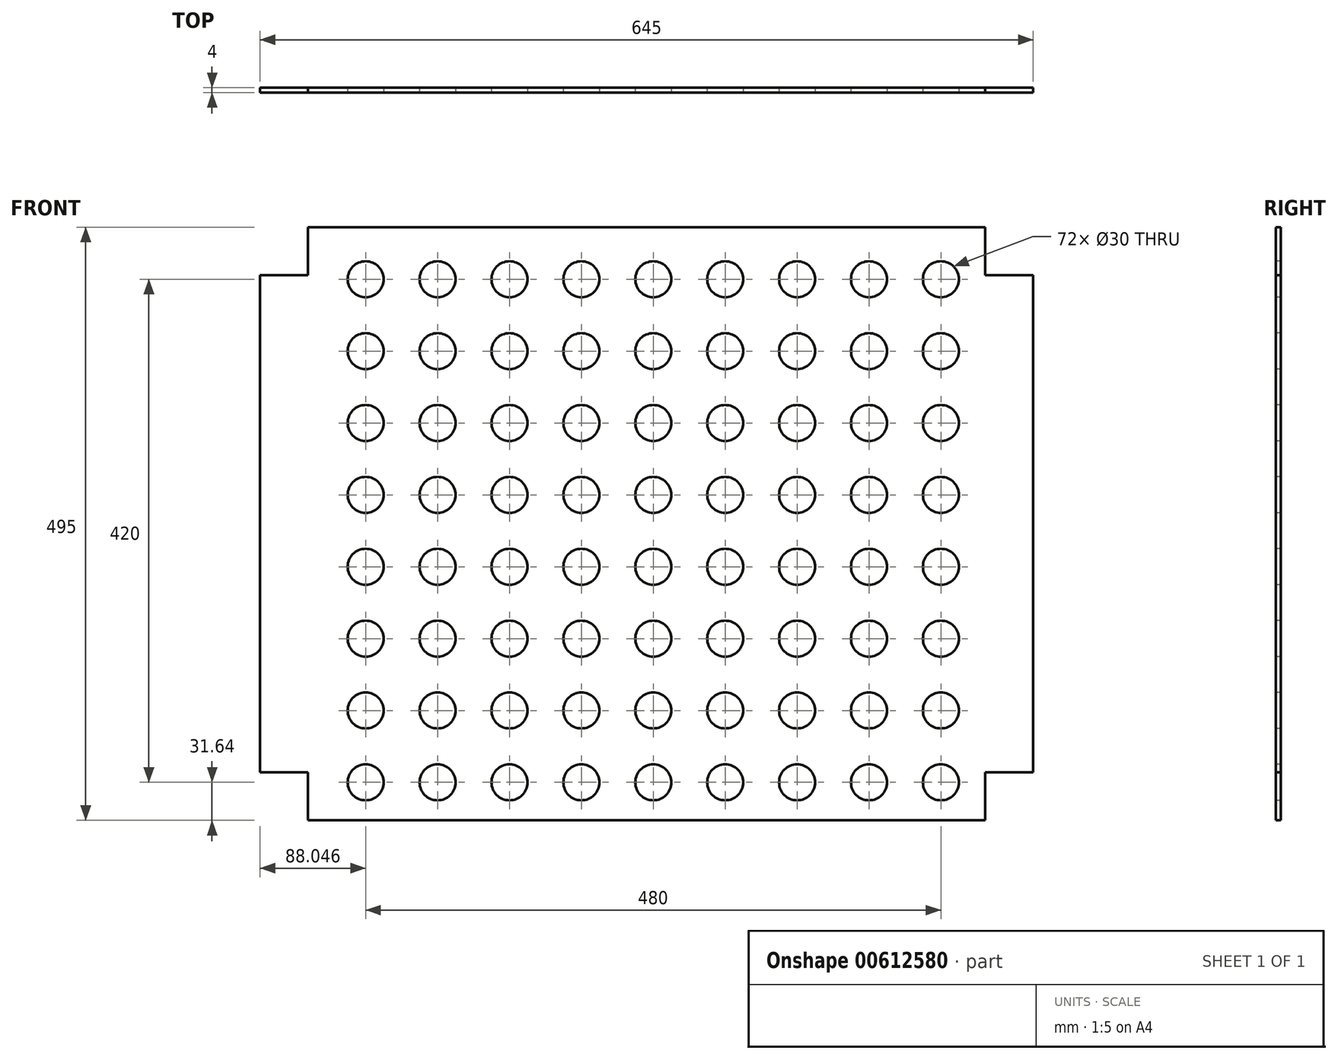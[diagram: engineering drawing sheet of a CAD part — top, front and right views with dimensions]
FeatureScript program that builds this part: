
annotation { "Feature Type Name" : "Feature", "Feature Type Description" : "" }
export const myFeature = defineFeature(function(context is Context, id is Id, definition is map)
    precondition{}
    {
        {
            var Q0;
            Q0=qCreatedBy(makeId("Front.planeOp"),FACE);
            var sketch = newSketch(context, id + "F0", { "sketchPlane" : qUnion([Q0])});
            skLineSegment(sketch, "E0", {"start": v(0, 247.5) * mm, "end": v(-282.5, 247.5) * mm});
            skLineSegment(sketch, "E1", {"start": v(-282.5, 247.5) * mm, "end": v(-282.5, 207.5) * mm});
            skLineSegment(sketch, "E2", {"start": v(-282.5, 207.5) * mm, "end": v(-322.5, 207.5) * mm});
            skLineSegment(sketch, "E3", {"start": v(-322.5, 207.5) * mm, "end": v(-322.5, 0) * mm});
            skLineSegment(sketch, "E4.MirrorCS", {"start": v(0, 247.5) * mm, "end": v(282.5, 247.5) * mm});
            skLineSegment(sketch, "E5.MirrorCS", {"start": v(282.5, 247.5) * mm, "end": v(282.5, 207.5) * mm});
            skLineSegment(sketch, "E6.MirrorCS", {"start": v(282.5, 207.5) * mm, "end": v(322.5, 207.5) * mm});
            skLineSegment(sketch, "E7.MirrorCS", {"start": v(322.5, 207.5) * mm, "end": v(322.5, 0) * mm});
            skLineSegment(sketch, "E8.MirrorCS", {"start": v(-322.5, -207.5) * mm, "end": v(-322.5, 0) * mm});
            skLineSegment(sketch, "E9.MirrorCS", {"start": v(-282.5, -207.5) * mm, "end": v(-322.5, -207.5) * mm});
            skLineSegment(sketch, "E10.MirrorCS", {"start": v(-282.5, -247.5) * mm, "end": v(-282.5, -207.5) * mm});
            skLineSegment(sketch, "E11.MirrorCS", {"start": v(0, -247.5) * mm, "end": v(-282.5, -247.5) * mm});
            skLineSegment(sketch, "E12.MirrorCS", {"start": v(0, -247.5) * mm, "end": v(282.5, -247.5) * mm});
            skLineSegment(sketch, "E13.MirrorCS", {"start": v(282.5, -247.5) * mm, "end": v(282.5, -207.5) * mm});
            skLineSegment(sketch, "E14.MirrorCS", {"start": v(282.5, -207.5) * mm, "end": v(322.5, -207.5) * mm});
            skLineSegment(sketch, "E15.MirrorCS", {"start": v(322.5, -207.5) * mm, "end": v(322.5, 0) * mm});
            skSolve(sketch);
        }
        {
            var Q0;
            Q0=makeQuery(id+"F0.imprint","IMPRINT",FACE,{"disambiguationData":[TD([[makeQuery(id+"F0.imprint","IMPRINT",EDGE,{"derivedFrom":sQuery(id+"F0.wireOp",EDGE,"E0")}),1.0]])]});
            extrude(context, id + "F1", {"entities" : qUnion([Q0]), "depth" : 4 * mm, "offsetDistance" : 25.4 * mm});
        }
        {
            var Q0;
            Q0=makeQuery(id+"F1.opExtrude","CAP_FACE",FACE,{"disambiguationData":[OSD([sQuery(id+"F0.wireOp",EDGE,"E0"),sQuery(id+"F0.wireOp",EDGE,"E1"),sQuery(id+"F0.wireOp",EDGE,"E2"),sQuery(id+"F0.wireOp",EDGE,"E3"),sQuery(id+"F0.wireOp",EDGE,"E4.MirrorCS"),sQuery(id+"F0.wireOp",EDGE,"E5.MirrorCS"),sQuery(id+"F0.wireOp",EDGE,"E6.MirrorCS"),sQuery(id+"F0.wireOp",EDGE,"E7.MirrorCS"),sQuery(id+"F0.wireOp",EDGE,"E8.MirrorCS"),sQuery(id+"F0.wireOp",EDGE,"E9.MirrorCS"),sQuery(id+"F0.wireOp",EDGE,"E10.MirrorCS"),sQuery(id+"F0.wireOp",EDGE,"E11.MirrorCS"),sQuery(id+"F0.wireOp",EDGE,"E12.MirrorCS"),sQuery(id+"F0.wireOp",EDGE,"E13.MirrorCS"),sQuery(id+"F0.wireOp",EDGE,"E14.MirrorCS"),sQuery(id+"F0.wireOp",EDGE,"E15.MirrorCS")])],"isStart":false});
            var sketch = newSketch(context, id + "F2", { "sketchPlane" : qUnion([Q0])});
            skCircle(sketch, "E16", {"center": v(245.55, -215.86) * mm, "radius": 15 * mm});
            skCircle(sketch, "E17.0.1.0", {"center": v(245.55, -155.86) * mm, "radius": 15 * mm});
            skCircle(sketch, "E17.0.2.0", {"center": v(245.55, -95.86) * mm, "radius": 15 * mm});
            skCircle(sketch, "E17.0.3.0", {"center": v(245.55, -35.86) * mm, "radius": 15 * mm});
            skCircle(sketch, "E17.0.4.0", {"center": v(245.55, 24.14) * mm, "radius": 15 * mm});
            skCircle(sketch, "E17.0.5.0", {"center": v(245.55, 84.14) * mm, "radius": 15 * mm});
            skCircle(sketch, "E17.0.6.0", {"center": v(245.55, 144.14) * mm, "radius": 15 * mm});
            skCircle(sketch, "E17.0.7.0", {"center": v(245.55, 204.14) * mm, "radius": 15 * mm});
            skCircle(sketch, "E17.1.0.0", {"center": v(185.55, -215.86) * mm, "radius": 15 * mm});
            skCircle(sketch, "E17.1.1.0", {"center": v(185.55, -155.86) * mm, "radius": 15 * mm});
            skCircle(sketch, "E17.1.2.0", {"center": v(185.55, -95.86) * mm, "radius": 15 * mm});
            skCircle(sketch, "E17.1.3.0", {"center": v(185.55, -35.86) * mm, "radius": 15 * mm});
            skCircle(sketch, "E17.1.4.0", {"center": v(185.55, 24.14) * mm, "radius": 15 * mm});
            skCircle(sketch, "E17.1.5.0", {"center": v(185.55, 84.14) * mm, "radius": 15 * mm});
            skCircle(sketch, "E17.1.6.0", {"center": v(185.55, 144.14) * mm, "radius": 15 * mm});
            skCircle(sketch, "E17.1.7.0", {"center": v(185.55, 204.14) * mm, "radius": 15 * mm});
            skCircle(sketch, "E17.2.0.0", {"center": v(125.55, -215.86) * mm, "radius": 15 * mm});
            skCircle(sketch, "E17.2.1.0", {"center": v(125.55, -155.86) * mm, "radius": 15 * mm});
            skCircle(sketch, "E17.2.2.0", {"center": v(125.55, -95.86) * mm, "radius": 15 * mm});
            skCircle(sketch, "E17.2.3.0", {"center": v(125.55, -35.86) * mm, "radius": 15 * mm});
            skCircle(sketch, "E17.2.4.0", {"center": v(125.55, 24.14) * mm, "radius": 15 * mm});
            skCircle(sketch, "E17.2.5.0", {"center": v(125.55, 84.14) * mm, "radius": 15 * mm});
            skCircle(sketch, "E17.2.6.0", {"center": v(125.55, 144.14) * mm, "radius": 15 * mm});
            skCircle(sketch, "E17.2.7.0", {"center": v(125.55, 204.14) * mm, "radius": 15 * mm});
            skCircle(sketch, "E17.3.0.0", {"center": v(65.55, -215.86) * mm, "radius": 15 * mm});
            skCircle(sketch, "E17.3.1.0", {"center": v(65.55, -155.86) * mm, "radius": 15 * mm});
            skCircle(sketch, "E17.3.2.0", {"center": v(65.55, -95.86) * mm, "radius": 15 * mm});
            skCircle(sketch, "E17.3.3.0", {"center": v(65.55, -35.86) * mm, "radius": 15 * mm});
            skCircle(sketch, "E17.3.4.0", {"center": v(65.55, 24.14) * mm, "radius": 15 * mm});
            skCircle(sketch, "E17.3.5.0", {"center": v(65.55, 84.14) * mm, "radius": 15 * mm});
            skCircle(sketch, "E17.3.6.0", {"center": v(65.55, 144.14) * mm, "radius": 15 * mm});
            skCircle(sketch, "E17.3.7.0", {"center": v(65.55, 204.14) * mm, "radius": 15 * mm});
            skCircle(sketch, "E17.4.0.0", {"center": v(5.55, -215.86) * mm, "radius": 15 * mm});
            skCircle(sketch, "E17.4.1.0", {"center": v(5.55, -155.86) * mm, "radius": 15 * mm});
            skCircle(sketch, "E17.4.2.0", {"center": v(5.55, -95.86) * mm, "radius": 15 * mm});
            skCircle(sketch, "E17.4.3.0", {"center": v(5.55, -35.86) * mm, "radius": 15 * mm});
            skCircle(sketch, "E17.4.4.0", {"center": v(5.55, 24.14) * mm, "radius": 15 * mm});
            skCircle(sketch, "E17.4.5.0", {"center": v(5.55, 84.14) * mm, "radius": 15 * mm});
            skCircle(sketch, "E17.4.6.0", {"center": v(5.55, 144.14) * mm, "radius": 15 * mm});
            skCircle(sketch, "E17.4.7.0", {"center": v(5.55, 204.14) * mm, "radius": 15 * mm});
            skCircle(sketch, "E17.5.0.0", {"center": v(-54.45, -215.86) * mm, "radius": 15 * mm});
            skCircle(sketch, "E17.5.1.0", {"center": v(-54.45, -155.86) * mm, "radius": 15 * mm});
            skCircle(sketch, "E17.5.2.0", {"center": v(-54.45, -95.86) * mm, "radius": 15 * mm});
            skCircle(sketch, "E17.5.3.0", {"center": v(-54.45, -35.86) * mm, "radius": 15 * mm});
            skCircle(sketch, "E17.5.4.0", {"center": v(-54.45, 24.14) * mm, "radius": 15 * mm});
            skCircle(sketch, "E17.5.5.0", {"center": v(-54.45, 84.14) * mm, "radius": 15 * mm});
            skCircle(sketch, "E17.5.6.0", {"center": v(-54.45, 144.14) * mm, "radius": 15 * mm});
            skCircle(sketch, "E17.5.7.0", {"center": v(-54.45, 204.14) * mm, "radius": 15 * mm});
            skCircle(sketch, "E17.6.0.0", {"center": v(-114.45, -215.86) * mm, "radius": 15 * mm});
            skCircle(sketch, "E17.6.1.0", {"center": v(-114.45, -155.86) * mm, "radius": 15 * mm});
            skCircle(sketch, "E17.6.2.0", {"center": v(-114.45, -95.86) * mm, "radius": 15 * mm});
            skCircle(sketch, "E17.6.3.0", {"center": v(-114.45, -35.86) * mm, "radius": 15 * mm});
            skCircle(sketch, "E17.6.4.0", {"center": v(-114.45, 24.14) * mm, "radius": 15 * mm});
            skCircle(sketch, "E17.6.5.0", {"center": v(-114.45, 84.14) * mm, "radius": 15 * mm});
            skCircle(sketch, "E17.6.6.0", {"center": v(-114.45, 144.14) * mm, "radius": 15 * mm});
            skCircle(sketch, "E17.6.7.0", {"center": v(-114.45, 204.14) * mm, "radius": 15 * mm});
            skCircle(sketch, "E17.7.0.0", {"center": v(-174.45, -215.86) * mm, "radius": 15 * mm});
            skCircle(sketch, "E17.7.1.0", {"center": v(-174.45, -155.86) * mm, "radius": 15 * mm});
            skCircle(sketch, "E17.7.2.0", {"center": v(-174.45, -95.86) * mm, "radius": 15 * mm});
            skCircle(sketch, "E17.7.3.0", {"center": v(-174.45, -35.86) * mm, "radius": 15 * mm});
            skCircle(sketch, "E17.7.4.0", {"center": v(-174.45, 24.14) * mm, "radius": 15 * mm});
            skCircle(sketch, "E17.7.5.0", {"center": v(-174.45, 84.14) * mm, "radius": 15 * mm});
            skCircle(sketch, "E17.7.6.0", {"center": v(-174.45, 144.14) * mm, "radius": 15 * mm});
            skCircle(sketch, "E17.7.7.0", {"center": v(-174.45, 204.14) * mm, "radius": 15 * mm});
            skCircle(sketch, "E17.8.0.0", {"center": v(-234.45, -215.86) * mm, "radius": 15 * mm});
            skCircle(sketch, "E17.8.1.0", {"center": v(-234.45, -155.86) * mm, "radius": 15 * mm});
            skCircle(sketch, "E17.8.2.0", {"center": v(-234.45, -95.86) * mm, "radius": 15 * mm});
            skCircle(sketch, "E17.8.3.0", {"center": v(-234.45, -35.86) * mm, "radius": 15 * mm});
            skCircle(sketch, "E17.8.4.0", {"center": v(-234.45, 24.14) * mm, "radius": 15 * mm});
            skCircle(sketch, "E17.8.5.0", {"center": v(-234.45, 84.14) * mm, "radius": 15 * mm});
            skCircle(sketch, "E17.8.6.0", {"center": v(-234.45, 144.14) * mm, "radius": 15 * mm});
            skCircle(sketch, "E17.8.7.0", {"center": v(-234.45, 204.14) * mm, "radius": 15 * mm});
            skLineSegment(sketch, "E17.direction1", {"start": v(245.55, -215.86) * mm, "end": v(185.55, -215.86) * mm, "construction": true});
            skLineSegment(sketch, "E17.direction2", {"start": v(245.55, -215.86) * mm, "end": v(245.55, -155.86) * mm, "construction": true});
            skSolve(sketch);
        }
        {
            var Q0;
            Q0 = qSketchRegion(id + "F2", true);
            extrude(context, id + "F3", {"entities" : qUnion([Q0]), "operationType" : NewBodyOperationType.REMOVE, "oppositeDirection" : true, "depth" : 5 * mm, "offsetDistance" : 25.4 * mm});
        }
    });
